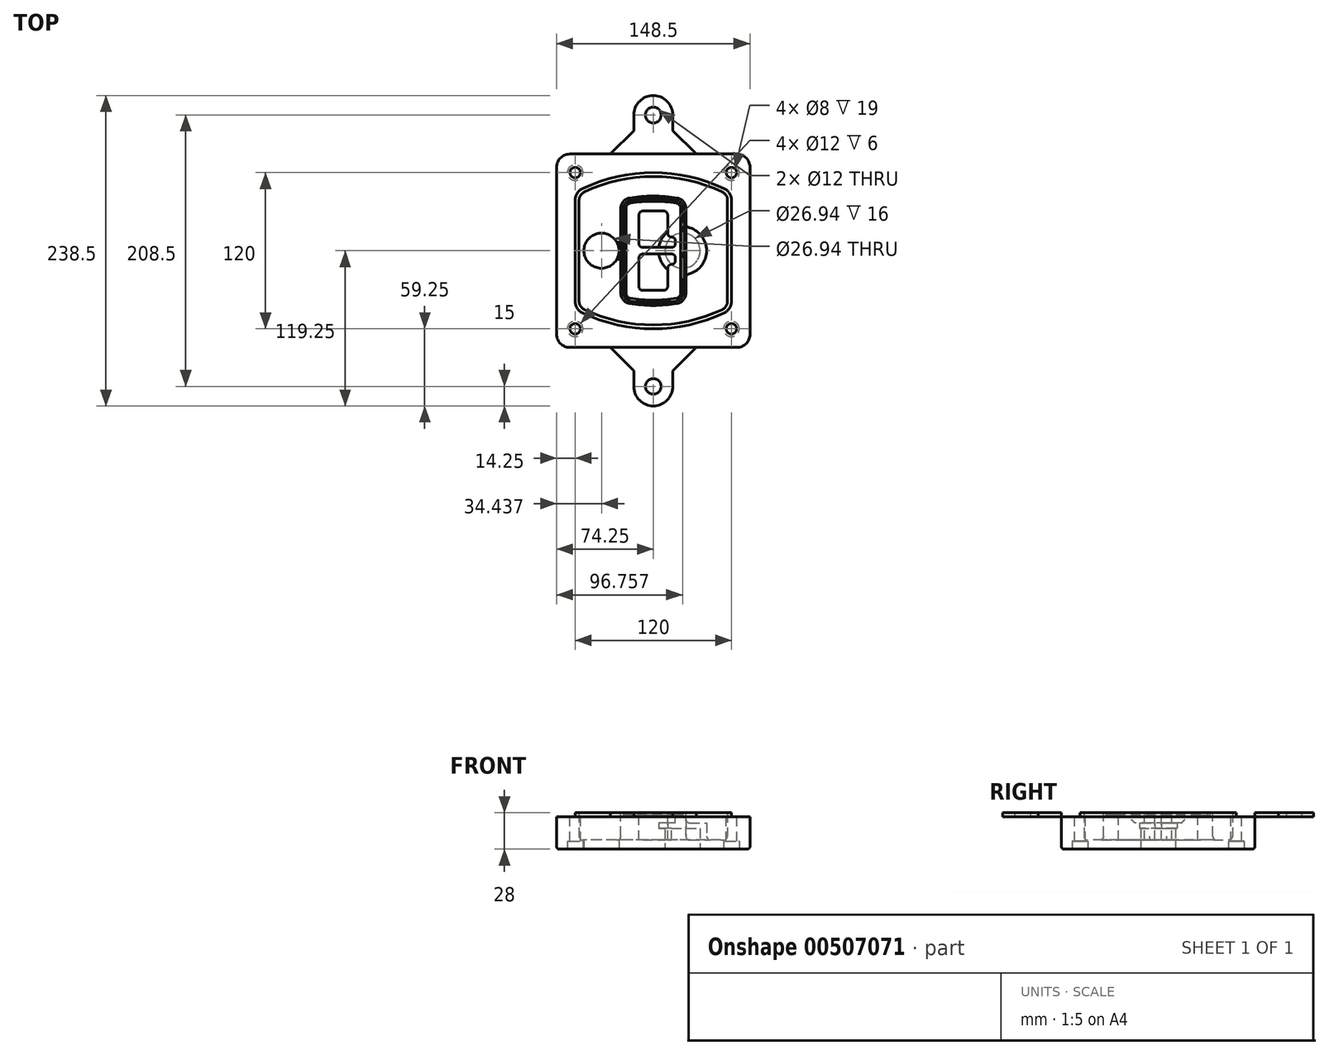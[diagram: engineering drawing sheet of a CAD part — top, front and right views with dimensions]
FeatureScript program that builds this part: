
annotation { "Feature Type Name" : "Feature", "Feature Type Description" : "" }
export const myFeature = defineFeature(function(context is Context, id is Id, definition is map)
    precondition{}
    {
        {
            var Q0;
            Q0=qCreatedBy(makeId("Top.planeOp"),FACE);
            var sketch = newSketch(context, id + "F0", { "sketchPlane" : qUnion([Q0])});
            skPoint(sketch, "E0.rect.middle", {"position": v(0, 0) * mm});
            skLineSegment(sketch, "E1.bottom", {"start": v(-64.25, -74.25) * mm, "end": v(64.25, -74.25) * mm});
            skLineSegment(sketch, "E1.top", {"start": v(-64.25, 74.25) * mm, "end": v(64.25, 74.25) * mm});
            skLineSegment(sketch, "E1.left", {"start": v(-74.25, -64.25) * mm, "end": v(-74.25, 64.25) * mm});
            skLineSegment(sketch, "E1.right", {"start": v(74.25, -64.25) * mm, "end": v(74.25, 64.25) * mm});
            skLineSegment(sketch, "E2", {"start": v(-74.25, 74.25) * mm, "end": v(74.25, -74.25) * mm, "construction": true});
            skLineSegment(sketch, "E3", {"start": v(74.25, 74.25) * mm, "end": v(-74.25, -74.25) * mm, "construction": true});
            skCircle(sketch, "E4", {"center": v(-60, 60) * mm, "radius": 4 * mm});
            skCircle(sketch, "E5", {"center": v(60, 60) * mm, "radius": 4 * mm});
            skCircle(sketch, "E6", {"center": v(60, -60) * mm, "radius": 4 * mm});
            skCircle(sketch, "E7", {"center": v(-60, -60) * mm, "radius": 4 * mm});
            skLineSegment(sketch, "E8", {"start": v(-60, 60) * mm, "end": v(60, 60) * mm, "construction": true});
            skLineSegment(sketch, "E9", {"start": v(60, 60) * mm, "end": v(60, -60) * mm, "construction": true});
            skLineSegment(sketch, "E10", {"start": v(60, -60) * mm, "end": v(-60, -60) * mm, "construction": true});
            skLineSegment(sketch, "E11", {"start": v(-60, -60) * mm, "end": v(-60, 60) * mm, "construction": true});
            skLineSegment(sketch, "E12", {"start": v(-60, 38.83) * mm, "end": v(-60, -38.83) * mm});
            skLineSegment(sketch, "E13", {"start": v(60, 38.83) * mm, "end": v(60, -38.83) * mm});
            skArc(sketch, "E14", {"start": v(54.26, 47.88) * mm, "mid": v(0, 60) * mm, "end": v(-54.26, 47.88) * mm});
            skArc(sketch, "E15", {"start": v(-54.26, -47.88) * mm, "mid": v(0, -60) * mm, "end": v(54.26, -47.88) * mm});
            skLineSegment(sketch, "E16", {"start": v(-60, 0) * mm, "end": v(60, 0) * mm, "construction": true});
            skPoint(sketch, "E17.visualSharp", {"position": v(-60, -45) * mm});
            skArc(sketch, "E17.filletArc", {"start": v(-60, -38.83) * mm, "mid": v(-58.44, -44.2) * mm, "end": v(-54.26, -47.88) * mm});
            skPoint(sketch, "E18.visualSharp", {"position": v(-60, 45) * mm});
            skArc(sketch, "E18.filletArc", {"start": v(-54.26, 47.88) * mm, "mid": v(-58.44, 44.2) * mm, "end": v(-60, 38.83) * mm});
            skPoint(sketch, "E19.visualSharp", {"position": v(60, 45) * mm});
            skArc(sketch, "E19.filletArc", {"start": v(60, 38.83) * mm, "mid": v(58.44, 44.2) * mm, "end": v(54.26, 47.88) * mm});
            skPoint(sketch, "E20.visualSharp", {"position": v(60, -45) * mm});
            skArc(sketch, "E20.filletArc", {"start": v(54.26, -47.88) * mm, "mid": v(58.44, -44.2) * mm, "end": v(60, -38.83) * mm});
            skPoint(sketch, "E21.visualSharp", {"position": v(-74.25, 74.25) * mm});
            skArc(sketch, "E21.filletArc", {"start": v(-64.25, 74.25) * mm, "mid": v(-71.32, 71.32) * mm, "end": v(-74.25, 64.25) * mm});
            skPoint(sketch, "E22.visualSharp", {"position": v(74.25, 74.25) * mm});
            skArc(sketch, "E22.filletArc", {"start": v(74.25, 64.25) * mm, "mid": v(71.32, 71.32) * mm, "end": v(64.25, 74.25) * mm});
            skPoint(sketch, "E23.visualSharp", {"position": v(74.25, -74.25) * mm});
            skArc(sketch, "E23.filletArc", {"start": v(64.25, -74.25) * mm, "mid": v(71.32, -71.32) * mm, "end": v(74.25, -64.25) * mm});
            skPoint(sketch, "E24.visualSharp", {"position": v(-74.25, -74.25) * mm});
            skArc(sketch, "E24.filletArc", {"start": v(-74.25, -64.25) * mm, "mid": v(-71.32, -71.32) * mm, "end": v(-64.25, -74.25) * mm});
            skArc(sketch, "E25.0", {"start": v(57, 38.83) * mm, "mid": v(55.9, 42.58) * mm, "end": v(52.98, 45.17) * mm});
            skLineSegment(sketch, "E25.1", {"start": v(57, 38.83) * mm, "end": v(57, -38.83) * mm});
            skArc(sketch, "E25.2", {"start": v(52.98, -45.17) * mm, "mid": v(55.9, -42.58) * mm, "end": v(57, -38.83) * mm});
            skArc(sketch, "E25.3", {"start": v(-52.98, -45.17) * mm, "mid": v(0, -57) * mm, "end": v(52.98, -45.17) * mm});
            skArc(sketch, "E25.4", {"start": v(-57, -38.83) * mm, "mid": v(-55.9, -42.58) * mm, "end": v(-52.98, -45.17) * mm});
            skArc(sketch, "E25.5", {"start": v(52.98, 45.17) * mm, "mid": v(0, 57) * mm, "end": v(-52.98, 45.17) * mm});
            skLineSegment(sketch, "E25.6", {"start": v(-57, 38.83) * mm, "end": v(-57, -38.83) * mm});
            skArc(sketch, "E25.7", {"start": v(-52.98, 45.17) * mm, "mid": v(-55.9, 42.58) * mm, "end": v(-57, 38.83) * mm});
            skArc(sketch, "E26.0", {"start": v(-55.96, 51.5) * mm, "mid": v(-61.82, 46.33) * mm, "end": v(-64, 38.83) * mm});
            skArc(sketch, "E26.1", {"start": v(55.96, 51.5) * mm, "mid": v(0, 64) * mm, "end": v(-55.96, 51.5) * mm});
            skArc(sketch, "E26.2", {"start": v(64, 38.83) * mm, "mid": v(61.82, 46.33) * mm, "end": v(55.96, 51.5) * mm});
            skLineSegment(sketch, "E26.3", {"start": v(64, 38.83) * mm, "end": v(64, -38.83) * mm});
            skArc(sketch, "E26.4", {"start": v(55.96, -51.5) * mm, "mid": v(61.82, -46.33) * mm, "end": v(64, -38.83) * mm});
            skLineSegment(sketch, "E26.5", {"start": v(-64, 38.83) * mm, "end": v(-64, -38.83) * mm});
            skArc(sketch, "E26.6", {"start": v(-55.96, -51.5) * mm, "mid": v(0, -64) * mm, "end": v(55.96, -51.5) * mm});
            skArc(sketch, "E26.7", {"start": v(-64, -38.83) * mm, "mid": v(-61.82, -46.33) * mm, "end": v(-55.96, -51.5) * mm});
            skSolve(sketch);
        }
        {
            var Q0;
            Q0=makeQuery(id+"F0.imprint","IMPRINT",FACE,{"disambiguationData":[TD([[makeQuery(id+"F0.imprint","IMPRINT",EDGE,{"derivedFrom":sQuery(id+"F0.wireOp",EDGE,"E1.bottom")}),1.0]])]});
            var Q1;
            Q1=makeQuery(id+"F0.imprint","IMPRINT",FACE,{"disambiguationData":[TD([[makeQuery(id+"F0.imprint","IMPRINT",EDGE,{"derivedFrom":sQuery(id+"F0.wireOp",EDGE,"E12")}),1.0]])]});
            var Q2;
            Q2=makeQuery(id+"F0.imprint","IMPRINT",FACE,{"disambiguationData":[TD([[makeQuery(id+"F0.imprint","IMPRINT",EDGE,{"derivedFrom":sQuery(id+"F0.wireOp",EDGE,"E25.0")}),1.0]])]});
            var Q3;
            Q3=makeQuery(id+"F0.imprint","IMPRINT",FACE,{"disambiguationData":[TD([[makeQuery(id+"F0.imprint","IMPRINT",EDGE,{"derivedFrom":sQuery(id+"F0.wireOp",EDGE,"E12")}),-1.0]])]});
            extrude(context, id + "F1", {"entities" : qUnion([Q0, Q1, Q2, Q3]), "oppositeDirection" : true, "depth" : 25 * mm});
        }
        {
            var Q0;
            Q0=makeQuery(id+"F0.imprint","IMPRINT",FACE,{"disambiguationData":[TD([[makeQuery(id+"F0.imprint","IMPRINT",EDGE,{"derivedFrom":sQuery(id+"F0.wireOp",EDGE,"E12")}),1.0]])]});
            extrude(context, id + "F2", {"entities" : qUnion([Q0]), "operationType" : NewBodyOperationType.ADD, "depth" : 3 * mm});
        }
        {
            var Q0;
            Q0=makeQuery(id+"F0.imprint","IMPRINT",FACE,{"disambiguationData":[TD([[makeQuery(id+"F0.imprint","IMPRINT",EDGE,{"derivedFrom":sQuery(id+"F0.wireOp",EDGE,"E25.0")}),1.0]])]});
            extrude(context, id + "F3", {"entities" : qUnion([Q0]), "operationType" : NewBodyOperationType.REMOVE, "oppositeDirection" : true, "depth" : 18 * mm});
        }
        {
            var Q0;
            Q0=makeQuery(id+"F2.opExtrude","CAP_FACE",FACE,{"disambiguationData":[OSD([sQuery(id+"F0.wireOp",EDGE,"E12"),sQuery(id+"F0.wireOp",EDGE,"E13"),sQuery(id+"F0.wireOp",EDGE,"E14"),sQuery(id+"F0.wireOp",EDGE,"E15"),sQuery(id+"F0.wireOp",EDGE,"E17.filletArc"),sQuery(id+"F0.wireOp",EDGE,"E18.filletArc"),sQuery(id+"F0.wireOp",EDGE,"E19.filletArc"),sQuery(id+"F0.wireOp",EDGE,"E20.filletArc"),sQuery(id+"F0.wireOp",EDGE,"E25.0"),sQuery(id+"F0.wireOp",EDGE,"E25.1"),sQuery(id+"F0.wireOp",EDGE,"E25.2"),sQuery(id+"F0.wireOp",EDGE,"E25.3"),sQuery(id+"F0.wireOp",EDGE,"E25.4"),sQuery(id+"F0.wireOp",EDGE,"E25.5"),sQuery(id+"F0.wireOp",EDGE,"E25.6"),sQuery(id+"F0.wireOp",EDGE,"E25.7")])],"isStart":false});
            var sketch = newSketch(context, id + "F4", { "sketchPlane" : qUnion([Q0])});
            skArc(sketch, "E27.0", {"start": v(-18.34, -40.45) * mm, "mid": v(0, -42) * mm, "end": v(18.34, -40.45) * mm});
            skArc(sketch, "E28.0", {"start": v(18.34, 40.45) * mm, "mid": v(0, 42) * mm, "end": v(-18.34, 40.45) * mm});
            skLineSegment(sketch, "E29", {"start": v(-25, 32.57) * mm, "end": v(-25, -32.57) * mm});
            skLineSegment(sketch, "E30", {"start": v(25, 32.57) * mm, "end": v(25, -32.57) * mm});
            skLineSegment(sketch, "E31", {"start": v(-25, 39.1) * mm, "end": v(25, 39.1) * mm, "construction": true});
            skLineSegment(sketch, "E32", {"start": v(-25, -39.1) * mm, "end": v(25, -39.1) * mm, "construction": true});
            skPoint(sketch, "E33.visualSharp", {"position": v(-25, 39.1) * mm});
            skArc(sketch, "E33.filletArc", {"start": v(-18.34, 40.45) * mm, "mid": v(-23.11, 37.73) * mm, "end": v(-25, 32.57) * mm});
            skPoint(sketch, "E34.visualSharp", {"position": v(25, 39.1) * mm});
            skArc(sketch, "E34.filletArc", {"start": v(25, 32.57) * mm, "mid": v(23.11, 37.73) * mm, "end": v(18.34, 40.45) * mm});
            skPoint(sketch, "E35.visualSharp", {"position": v(25, -39.1) * mm});
            skArc(sketch, "E35.filletArc", {"start": v(18.34, -40.45) * mm, "mid": v(23.11, -37.73) * mm, "end": v(25, -32.57) * mm});
            skPoint(sketch, "E36.visualSharp", {"position": v(-25, -39.1) * mm});
            skArc(sketch, "E36.filletArc", {"start": v(-25, -32.57) * mm, "mid": v(-23.11, -37.73) * mm, "end": v(-18.34, -40.45) * mm});
            skArc(sketch, "E37.0", {"start": v(52.98, 45.17) * mm, "mid": v(0, 57) * mm, "end": v(-52.98, 45.17) * mm});
            skArc(sketch, "E37.1", {"start": v(-52.98, 45.17) * mm, "mid": v(-55.9, 42.58) * mm, "end": v(-57, 38.83) * mm});
            skLineSegment(sketch, "E37.2", {"start": v(-57, 38.83) * mm, "end": v(-57, -38.83) * mm});
            skArc(sketch, "E37.3", {"start": v(-57, -38.83) * mm, "mid": v(-55.9, -42.58) * mm, "end": v(-52.98, -45.17) * mm});
            skArc(sketch, "E37.4", {"start": v(-52.98, -45.17) * mm, "mid": v(0, -57) * mm, "end": v(52.98, -45.17) * mm});
            skArc(sketch, "E37.5", {"start": v(52.98, -45.17) * mm, "mid": v(55.9, -42.58) * mm, "end": v(57, -38.83) * mm});
            skLineSegment(sketch, "E37.6", {"start": v(57, 38.83) * mm, "end": v(57, -38.83) * mm});
            skArc(sketch, "E37.7", {"start": v(57, 38.83) * mm, "mid": v(55.9, 42.58) * mm, "end": v(52.98, 45.17) * mm});
            skLineSegment(sketch, "E38.0", {"start": v(23, 32.57) * mm, "end": v(23, -32.57) * mm});
            skArc(sketch, "E38.1", {"start": v(18, -38.48) * mm, "mid": v(21.58, -36.44) * mm, "end": v(23, -32.57) * mm});
            skArc(sketch, "E38.2", {"start": v(-18, -38.48) * mm, "mid": v(0, -40) * mm, "end": v(18, -38.48) * mm});
            skArc(sketch, "E38.3", {"start": v(-23, -32.57) * mm, "mid": v(-21.58, -36.44) * mm, "end": v(-18, -38.48) * mm});
            skLineSegment(sketch, "E38.4", {"start": v(-23, 32.57) * mm, "end": v(-23, -32.57) * mm});
            skArc(sketch, "E38.5", {"start": v(23, 32.57) * mm, "mid": v(21.58, 36.44) * mm, "end": v(18, 38.48) * mm});
            skArc(sketch, "E38.6", {"start": v(-18, 38.48) * mm, "mid": v(-21.58, 36.44) * mm, "end": v(-23, 32.57) * mm});
            skArc(sketch, "E38.7", {"start": v(18, 38.48) * mm, "mid": v(0, 40) * mm, "end": v(-18, 38.48) * mm});
            skArc(sketch, "E39.0", {"start": v(21, 32.57) * mm, "mid": v(20.06, 35.15) * mm, "end": v(17.67, 36.5) * mm});
            skLineSegment(sketch, "E39.1", {"start": v(21, 32.57) * mm, "end": v(21, -32.57) * mm});
            skArc(sketch, "E39.2", {"start": v(17.67, -36.5) * mm, "mid": v(20.06, -35.15) * mm, "end": v(21, -32.57) * mm});
            skArc(sketch, "E39.3", {"start": v(-17.67, -36.5) * mm, "mid": v(0, -38) * mm, "end": v(17.67, -36.5) * mm});
            skArc(sketch, "E39.4", {"start": v(-21, -32.57) * mm, "mid": v(-20.06, -35.15) * mm, "end": v(-17.67, -36.5) * mm});
            skArc(sketch, "E39.5", {"start": v(17.67, 36.5) * mm, "mid": v(0, 38) * mm, "end": v(-17.67, 36.5) * mm});
            skLineSegment(sketch, "E39.6", {"start": v(-21, 32.57) * mm, "end": v(-21, -32.57) * mm});
            skArc(sketch, "E39.7", {"start": v(-17.67, 36.5) * mm, "mid": v(-20.06, 35.15) * mm, "end": v(-21, 32.57) * mm});
            skLineSegment(sketch, "E40", {"start": v(-25, 0) * mm, "end": v(25, 0) * mm, "construction": true});
            skLineSegment(sketch, "E41", {"start": v(-11, 5.5) * mm, "end": v(-11, 27.5) * mm});
            skLineSegment(sketch, "E42", {"start": v(-8, 30.5) * mm, "end": v(8, 30.5) * mm});
            skLineSegment(sketch, "E43", {"start": v(11, 27.5) * mm, "end": v(11, 13.5) * mm});
            skLineSegment(sketch, "E44", {"start": v(14, 10.5) * mm, "end": v(14, 10.5) * mm});
            skLineSegment(sketch, "E45", {"start": v(17, 7.5) * mm, "end": v(17, 5.5) * mm});
            skLineSegment(sketch, "E46", {"start": v(14, 2.5) * mm, "end": v(-8, 2.5) * mm});
            skPoint(sketch, "E47.visualSharp", {"position": v(-11, 30.5) * mm});
            skArc(sketch, "E47.filletArc", {"start": v(-8, 30.5) * mm, "mid": v(-10.12, 29.62) * mm, "end": v(-11, 27.5) * mm});
            skPoint(sketch, "E48.visualSharp", {"position": v(11, 30.5) * mm});
            skArc(sketch, "E48.filletArc", {"start": v(11, 27.5) * mm, "mid": v(10.12, 29.62) * mm, "end": v(8, 30.5) * mm});
            skPoint(sketch, "E49.visualSharp", {"position": v(11, 10.5) * mm});
            skArc(sketch, "E49.filletArc", {"start": v(11, 13.5) * mm, "mid": v(11.88, 11.38) * mm, "end": v(14, 10.5) * mm});
            skPoint(sketch, "E50.visualSharp", {"position": v(17, 10.5) * mm});
            skArc(sketch, "E50.filletArc", {"start": v(17, 7.5) * mm, "mid": v(16.12, 9.62) * mm, "end": v(14, 10.5) * mm});
            skPoint(sketch, "E51.visualSharp", {"position": v(17, 2.5) * mm});
            skArc(sketch, "E51.filletArc", {"start": v(14, 2.5) * mm, "mid": v(16.12, 3.38) * mm, "end": v(17, 5.5) * mm});
            skPoint(sketch, "E52.visualSharp", {"position": v(-11, 2.5) * mm});
            skArc(sketch, "E52.filletArc", {"start": v(-11, 5.5) * mm, "mid": v(-10.12, 3.38) * mm, "end": v(-8, 2.5) * mm});
            skLineSegment(sketch, "E53.0.MirrorCS", {"start": v(14, -2.5) * mm, "end": v(-8, -2.5) * mm});
            skArc(sketch, "E54.0.MirrorCS", {"start": v(-11, -5.5) * mm, "mid": v(-10.12, -3.38) * mm, "end": v(-8, -2.5) * mm});
            skLineSegment(sketch, "E55.0.MirrorCS", {"start": v(-11, -5.5) * mm, "end": v(-11, -27.5) * mm});
            skArc(sketch, "E56.0.MirrorCS", {"start": v(-8, -30.5) * mm, "mid": v(-10.12, -29.62) * mm, "end": v(-11, -27.5) * mm});
            skLineSegment(sketch, "E57.0.MirrorCS", {"start": v(-8, -30.5) * mm, "end": v(8, -30.5) * mm});
            skArc(sketch, "E58.0.MirrorCS", {"start": v(11, -27.5) * mm, "mid": v(10.12, -29.62) * mm, "end": v(8, -30.5) * mm});
            skLineSegment(sketch, "E59.0.MirrorCS", {"start": v(11, -27.5) * mm, "end": v(11, -13.5) * mm});
            skArc(sketch, "E60.0.MirrorCS", {"start": v(11, -13.5) * mm, "mid": v(11.88, -11.38) * mm, "end": v(14, -10.5) * mm});
            skArc(sketch, "E61.0.MirrorCS", {"start": v(17, -7.5) * mm, "mid": v(16.12, -9.62) * mm, "end": v(14, -10.5) * mm});
            skLineSegment(sketch, "E62.0.MirrorCS", {"start": v(17, -7.5) * mm, "end": v(17, -5.5) * mm});
            skArc(sketch, "E63.0.MirrorCS", {"start": v(14, -2.5) * mm, "mid": v(16.12, -3.38) * mm, "end": v(17, -5.5) * mm});
            skSolve(sketch);
        }
        {
            var Q0;
            Q0=makeQuery(id+"F4.imprint","IMPRINT",FACE,{"disambiguationData":[TD([[makeQuery(id+"F4.imprint","IMPRINT",EDGE,{"derivedFrom":sQuery(id+"F4.wireOp",EDGE,"E27.0")}),1.0]])]});
            var Q1;
            Q1=makeQuery(id+"F4.imprint","IMPRINT",FACE,{"disambiguationData":[TD([[makeQuery(id+"F4.imprint","IMPRINT",EDGE,{"derivedFrom":sQuery(id+"F4.wireOp",EDGE,"E38.0")}),-1.0]])]});
            var Q2;
            Q2=makeQuery(id+"F4.imprint","IMPRINT",FACE,{"disambiguationData":[TD([[makeQuery(id+"F4.imprint","IMPRINT",EDGE,{"derivedFrom":sQuery(id+"F4.wireOp",EDGE,"E39.0")}),1.0]])]});
            extrude(context, id + "F5", {"entities" : qUnion([Q0, Q1, Q2]), "operationType" : NewBodyOperationType.ADD, "endBound" : BoundingType.UP_TO_NEXT, "oppositeDirection" : true, "depth" : 25 * mm});
        }
        {
            var Q0;
            Q0=makeQuery(id+"F4.imprint","IMPRINT",FACE,{"disambiguationData":[TD([[makeQuery(id+"F4.imprint","IMPRINT",EDGE,{"derivedFrom":sQuery(id+"F4.wireOp",EDGE,"E38.0")}),-1.0]])]});
            extrude(context, id + "F6", {"entities" : qUnion([Q0]), "operationType" : NewBodyOperationType.REMOVE, "oppositeDirection" : true, "depth" : 2 * mm});
        }
        {
            var Q0;
            Q0=makeQuery(id+"F1.opExtrude","CAP_FACE",FACE,{"disambiguationData":[OSD([sQuery(id+"F0.wireOp",EDGE,"E1.bottom"),sQuery(id+"F0.wireOp",EDGE,"E1.top"),sQuery(id+"F0.wireOp",EDGE,"E1.left"),sQuery(id+"F0.wireOp",EDGE,"E1.right"),sQuery(id+"F0.wireOp",EDGE,"E4"),sQuery(id+"F0.wireOp",EDGE,"E5"),sQuery(id+"F0.wireOp",EDGE,"E6"),sQuery(id+"F0.wireOp",EDGE,"E7"),sQuery(id+"F0.wireOp",EDGE,"E21.filletArc"),sQuery(id+"F0.wireOp",EDGE,"E22.filletArc"),sQuery(id+"F0.wireOp",EDGE,"E23.filletArc"),sQuery(id+"F0.wireOp",EDGE,"E24.filletArc")])],"isStart":false});
            var sketch = newSketch(context, id + "F7", { "sketchPlane" : qUnion([Q0])});
            skCircle(sketch, "E64", {"center": v(22.5, 0) * mm, "radius": 13.47 * mm});
            skCircle(sketch, "E65", {"center": v(-39.81, 0) * mm, "radius": 13.47 * mm});
            skLineSegment(sketch, "E66", {"start": v(74.25, 0) * mm, "end": v(-74.25, 0) * mm});
            skCircle(sketch, "E67", {"center": v(22.5, 0) * mm, "radius": 18.47 * mm});
            skCircle(sketch, "E68", {"center": v(60, -60) * mm, "radius": 6 * mm});
            skCircle(sketch, "E69", {"center": v(-60, -60) * mm, "radius": 6 * mm});
            skCircle(sketch, "E70", {"center": v(-60, 60) * mm, "radius": 6 * mm});
            skCircle(sketch, "E71", {"center": v(60, 60) * mm, "radius": 6 * mm});
            skSolve(sketch);
        }
        {
            var Q0;
            {var subQ1=sQuery(id+"F7.wireOp",EDGE,"E66");var subQ4=sQuery(id+"F7.wireOp",EDGE,"E64");var subQ6=makeQuery(id+"F7.imprint","INTERSECT",VERTEX,{"disambiguationData":[OD(0.0)],"derivedFrom":[subQ4,subQ1]});Q0=makeQuery(id+"F7.imprint","IMPRINT",FACE,{"disambiguationData":[TD([[makeQuery(id+"F7.imprint","IMPRINT",EDGE,{"disambiguationData":[TD([[subQ6,-1.0]])],"derivedFrom":subQ4}),-1.0]])]});}
            var Q1;
            {var subQ0=sQuery(id+"F7.wireOp",EDGE,"E66");var subQ1=sQuery(id+"F7.wireOp",EDGE,"E64");var subQ3=makeQuery(id+"F7.imprint","INTERSECT",VERTEX,{"disambiguationData":[OD(0.0)],"derivedFrom":[subQ1,subQ0]});Q1=makeQuery(id+"F7.imprint","IMPRINT",FACE,{"disambiguationData":[TD([[makeQuery(id+"F7.imprint","IMPRINT",EDGE,{"disambiguationData":[TD([[subQ3,-1.0]])],"derivedFrom":subQ1}),1.0]])]});}
            var Q2;
            {var subQ0=sQuery(id+"F7.wireOp",EDGE,"E66");var subQ1=sQuery(id+"F7.wireOp",EDGE,"E64");var subQ3=makeQuery(id+"F7.imprint","INTERSECT",VERTEX,{"disambiguationData":[OD(0.0)],"derivedFrom":[subQ1,subQ0]});Q2=makeQuery(id+"F7.imprint","IMPRINT",FACE,{"disambiguationData":[TD([[makeQuery(id+"F7.imprint","IMPRINT",EDGE,{"disambiguationData":[TD([[subQ3,1.0]])],"derivedFrom":subQ1}),1.0]])]});}
            var Q3;
            {var subQ1=sQuery(id+"F7.wireOp",EDGE,"E66");var subQ4=sQuery(id+"F7.wireOp",EDGE,"E64");var subQ6=makeQuery(id+"F7.imprint","INTERSECT",VERTEX,{"disambiguationData":[OD(0.0)],"derivedFrom":[subQ4,subQ1]});Q3=makeQuery(id+"F7.imprint","IMPRINT",FACE,{"disambiguationData":[TD([[makeQuery(id+"F7.imprint","IMPRINT",EDGE,{"disambiguationData":[TD([[subQ6,1.0]])],"derivedFrom":subQ4}),-1.0]])]});}
            extrude(context, id + "F8", {"entities" : qUnion([Q0, Q1, Q2, Q3]), "operationType" : NewBodyOperationType.ADD, "oppositeDirection" : true, "depth" : 20 * mm});
        }
        {
            var Q0;
            {var subQ0=sQuery(id+"F7.wireOp",EDGE,"E66");var subQ1=sQuery(id+"F7.wireOp",EDGE,"E64");var subQ3=makeQuery(id+"F7.imprint","INTERSECT",VERTEX,{"disambiguationData":[OD(0.0)],"derivedFrom":[subQ1,subQ0]});Q0=makeQuery(id+"F7.imprint","IMPRINT",FACE,{"disambiguationData":[TD([[makeQuery(id+"F7.imprint","IMPRINT",EDGE,{"disambiguationData":[TD([[subQ3,-1.0]])],"derivedFrom":subQ1}),1.0]])]});}
            var Q1;
            {var subQ0=sQuery(id+"F7.wireOp",EDGE,"E66");var subQ1=sQuery(id+"F7.wireOp",EDGE,"E64");var subQ3=makeQuery(id+"F7.imprint","INTERSECT",VERTEX,{"disambiguationData":[OD(0.0)],"derivedFrom":[subQ1,subQ0]});Q1=makeQuery(id+"F7.imprint","IMPRINT",FACE,{"disambiguationData":[TD([[makeQuery(id+"F7.imprint","IMPRINT",EDGE,{"disambiguationData":[TD([[subQ3,1.0]])],"derivedFrom":subQ1}),1.0]])]});}
            extrude(context, id + "F9", {"entities" : qUnion([Q0, Q1]), "operationType" : NewBodyOperationType.REMOVE, "oppositeDirection" : true, "depth" : 16 * mm});
        }
        {
            var Q0;
            {var subQ0=sQuery(id+"F7.wireOp",EDGE,"E66");var subQ1=sQuery(id+"F7.wireOp",EDGE,"E65");var subQ3=makeQuery(id+"F7.imprint","INTERSECT",VERTEX,{"disambiguationData":[OD(0.0)],"derivedFrom":[subQ1,subQ0]});Q0=makeQuery(id+"F7.imprint","IMPRINT",FACE,{"disambiguationData":[TD([[makeQuery(id+"F7.imprint","IMPRINT",EDGE,{"disambiguationData":[TD([[subQ3,-1.0]])],"derivedFrom":subQ1}),1.0]])]});}
            var Q1;
            {var subQ0=sQuery(id+"F7.wireOp",EDGE,"E66");var subQ1=sQuery(id+"F7.wireOp",EDGE,"E65");var subQ3=makeQuery(id+"F7.imprint","INTERSECT",VERTEX,{"disambiguationData":[OD(0.0)],"derivedFrom":[subQ1,subQ0]});Q1=makeQuery(id+"F7.imprint","IMPRINT",FACE,{"disambiguationData":[TD([[makeQuery(id+"F7.imprint","IMPRINT",EDGE,{"disambiguationData":[TD([[subQ3,1.0]])],"derivedFrom":subQ1}),1.0]])]});}
            var Q2;
            {var subQ0=sQuery(id+"F0.wireOp",EDGE,"E21.filletArc");var subQ1=sQuery(id+"F0.wireOp",EDGE,"E7");var subQ2=sQuery(id+"F0.wireOp",EDGE,"E6");var subQ3=sQuery(id+"F0.wireOp",EDGE,"E5");var subQ4=sQuery(id+"F0.wireOp",EDGE,"E4");var subQ5=sQuery(id+"F0.wireOp",EDGE,"E22.filletArc");var subQ6=sQuery(id+"F0.wireOp",EDGE,"E1.bottom");var subQ7=sQuery(id+"F0.wireOp",EDGE,"E1.right");var subQ8=sQuery(id+"F0.wireOp",EDGE,"E1.top");var subQ9=sQuery(id+"F0.wireOp",EDGE,"E1.left");var subQ10=sQuery(id+"F0.wireOp",EDGE,"E23.filletArc");var subQ11=sQuery(id+"F0.wireOp",EDGE,"E24.filletArc");Q2=makeQuery(id+"F2.boolean.opBoolean","SPLIT",FACE,{"disambiguationData":[TD([makeQuery(id+"F1.opExtrude","SWEPT_FACE",FACE,{"disambiguationData":[OSD([subQ6])]})])],"derivedFrom":makeQuery(id+"F1.opExtrude","CAP_FACE",FACE,{"disambiguationData":[OSD([subQ6,subQ8,subQ9,subQ7,subQ4,subQ3,subQ2,subQ1,subQ0,subQ5,subQ10,subQ11])],"isStart":true})});}
            extrude(context, id + "F10", {"entities" : qUnion([Q0, Q1, Q2]), "operationType" : NewBodyOperationType.REMOVE, "oppositeDirection" : true, "depth" : 25 * mm});
        }
        {
            var Q0;
            Q0=makeQuery(id+"F7.imprint","IMPRINT",FACE,{"disambiguationData":[TD([[makeQuery(id+"F7.imprint","IMPRINT",EDGE,{"derivedFrom":sQuery(id+"F7.wireOp",EDGE,"E68")}),1.0]])]});
            var Q1;
            Q1=makeQuery(id+"F7.imprint","IMPRINT",FACE,{"disambiguationData":[TD([[makeQuery(id+"F7.imprint","IMPRINT",EDGE,{"derivedFrom":makeQuery(id+"F1.opExtrude","CAP_EDGE",EDGE,{"disambiguationData":[OSD([sQuery(id+"F0.wireOp",EDGE,"E5")])],"isStart":false})}),-1.0]])]});
            var Q2;
            Q2=makeQuery(id+"F7.imprint","IMPRINT",FACE,{"disambiguationData":[TD([[makeQuery(id+"F7.imprint","IMPRINT",EDGE,{"derivedFrom":sQuery(id+"F7.wireOp",EDGE,"E69")}),1.0]])]});
            var Q3;
            Q3=makeQuery(id+"F7.imprint","IMPRINT",FACE,{"disambiguationData":[TD([[makeQuery(id+"F7.imprint","IMPRINT",EDGE,{"derivedFrom":makeQuery(id+"F1.opExtrude","CAP_EDGE",EDGE,{"disambiguationData":[OSD([sQuery(id+"F0.wireOp",EDGE,"E4")])],"isStart":false})}),-1.0]])]});
            var Q4;
            Q4=makeQuery(id+"F7.imprint","IMPRINT",FACE,{"disambiguationData":[TD([[makeQuery(id+"F7.imprint","IMPRINT",EDGE,{"derivedFrom":sQuery(id+"F7.wireOp",EDGE,"E70")}),1.0]])]});
            var Q5;
            Q5=makeQuery(id+"F7.imprint","IMPRINT",FACE,{"disambiguationData":[TD([[makeQuery(id+"F7.imprint","IMPRINT",EDGE,{"derivedFrom":makeQuery(id+"F1.opExtrude","CAP_EDGE",EDGE,{"disambiguationData":[OSD([sQuery(id+"F0.wireOp",EDGE,"E7")])],"isStart":false})}),-1.0]])]});
            var Q6;
            Q6=makeQuery(id+"F7.imprint","IMPRINT",FACE,{"disambiguationData":[TD([[makeQuery(id+"F7.imprint","IMPRINT",EDGE,{"derivedFrom":sQuery(id+"F7.wireOp",EDGE,"E71")}),1.0]])]});
            var Q7;
            Q7=makeQuery(id+"F7.imprint","IMPRINT",FACE,{"disambiguationData":[TD([[makeQuery(id+"F7.imprint","IMPRINT",EDGE,{"derivedFrom":makeQuery(id+"F1.opExtrude","CAP_EDGE",EDGE,{"disambiguationData":[OSD([sQuery(id+"F0.wireOp",EDGE,"E6")])],"isStart":false})}),-1.0]])]});
            extrude(context, id + "F11", {"entities" : qUnion([Q0, Q1, Q2, Q3, Q4, Q5, Q6, Q7]), "operationType" : NewBodyOperationType.REMOVE, "oppositeDirection" : true, "depth" : 6 * mm});
        }
        {
            var Q0;
            Q0=makeQuery(id+"F9.boolean.opBoolean","COPY",FACE,{"derivedFrom":makeQuery(id+"F9.opExtrude","CAP_FACE",FACE,{"disambiguationData":[OSD([sQuery(id+"F7.wireOp",EDGE,"E64")])],"isStart":false})});
            var sketch = newSketch(context, id + "F12", { "sketchPlane" : qUnion([Q0])});
            skArc(sketch, "E72.0", {"start": v(11, 14.45) * mm, "mid": v(6.45, 9.13) * mm, "end": v(4.2, 2.5) * mm});
            skArc(sketch, "E72.1", {"start": v(4.2, -2.5) * mm, "mid": v(6.45, -9.13) * mm, "end": v(11, -14.45) * mm});
            skLineSegment(sketch, "E73", {"start": v(4.2, -2.5) * mm, "end": v(14, -2.5) * mm});
            skLineSegment(sketch, "E74.0", {"start": v(14, 2.5) * mm, "end": v(4.2, 2.5) * mm});
            skArc(sketch, "E74.1", {"start": v(14, 2.5) * mm, "mid": v(16.12, 3.38) * mm, "end": v(17, 5.5) * mm});
            skLineSegment(sketch, "E74.2", {"start": v(17, 7.5) * mm, "end": v(17, 5.5) * mm});
            skArc(sketch, "E74.3", {"start": v(17, 7.5) * mm, "mid": v(16.12, 9.62) * mm, "end": v(14, 10.5) * mm});
            skArc(sketch, "E74.4", {"start": v(11, 13.5) * mm, "mid": v(11.88, 11.38) * mm, "end": v(14, 10.5) * mm});
            skLineSegment(sketch, "E74.5", {"start": v(11, 14.45) * mm, "end": v(11, 13.5) * mm});
            skLineSegment(sketch, "E74.7", {"start": v(14, -2.5) * mm, "end": v(4.2, -2.5) * mm});
            skArc(sketch, "E74.8", {"start": v(14, -2.5) * mm, "mid": v(16.12, -3.38) * mm, "end": v(17, -5.5) * mm});
            skLineSegment(sketch, "E74.9", {"start": v(17, -7.5) * mm, "end": v(17, -5.5) * mm});
            skArc(sketch, "E74.10", {"start": v(17, -7.5) * mm, "mid": v(16.12, -9.62) * mm, "end": v(14, -10.5) * mm});
            skArc(sketch, "E74.11", {"start": v(11, -13.5) * mm, "mid": v(11.88, -11.38) * mm, "end": v(14, -10.5) * mm});
            skLineSegment(sketch, "E74.12", {"start": v(11, -14.45) * mm, "end": v(11, -13.5) * mm});
            skPoint(sketch, "E75.orphan", {"position": v(11, -27.5) * mm});
            skPoint(sketch, "E76.orphan", {"position": v(-8, -2.5) * mm});
            skPoint(sketch, "E77.orphan", {"position": v(-8, 2.5) * mm});
            skPoint(sketch, "E78.orphan", {"position": v(11, 27.5) * mm});
            skSolve(sketch);
        }
        {
            var Q0;
            {var subQ7=sQuery(id+"F12.wireOp",EDGE,"E72.0");var subQ14=sQuery(id+"F12.wireOp",EDGE,"E72.1");var subQ16=sQuery(id+"F12.wireOp",EDGE,"E74.1");var subQ18=sQuery(id+"F12.wireOp",EDGE,"E74.8");Q0=qUnion([makeQuery(id+"F12.imprint","IMPRINT",FACE,{"disambiguationData":[TD([[makeQuery(id+"F12.imprint","IMPRINT",EDGE,{"derivedFrom":subQ7}),1.0]])]}),makeQuery(id+"F12.imprint","IMPRINT",FACE,{"disambiguationData":[TD([[makeQuery(id+"F12.imprint","IMPRINT",EDGE,{"derivedFrom":subQ14}),1.0]])]}),makeQuery(id+"F12.imprint","IMPRINT",FACE,{"disambiguationData":[TD([[makeQuery(id+"F12.imprint","IMPRINT",EDGE,{"derivedFrom":subQ16}),1.0]])]}),makeQuery(id+"F12.imprint","IMPRINT",FACE,{"disambiguationData":[TD([[makeQuery(id+"F12.imprint","IMPRINT",EDGE,{"derivedFrom":subQ18}),-1.0]])]})]);}
            var Q1;
            Q1=makeQuery(id+"F5.boolean.opBoolean","SPLIT",FACE,{"disambiguationData":[TD([makeQuery(id+"F5.opExtrude","SWEPT_FACE",FACE,{"disambiguationData":[OSD([sQuery(id+"F4.wireOp",EDGE,"E41")])]})])],"derivedFrom":makeQuery(id+"F3.boolean.opBoolean","COPY",FACE,{"derivedFrom":makeQuery(id+"F3.opExtrude","CAP_FACE",FACE,{"disambiguationData":[OSD([sQuery(id+"F0.wireOp",EDGE,"E25.0"),sQuery(id+"F0.wireOp",EDGE,"E25.1"),sQuery(id+"F0.wireOp",EDGE,"E25.2"),sQuery(id+"F0.wireOp",EDGE,"E25.3"),sQuery(id+"F0.wireOp",EDGE,"E25.4"),sQuery(id+"F0.wireOp",EDGE,"E25.5"),sQuery(id+"F0.wireOp",EDGE,"E25.6"),sQuery(id+"F0.wireOp",EDGE,"E25.7")])],"isStart":false})})});
            extrude(context, id + "F13", {"entities" : qUnion([Q0]), "operationType" : NewBodyOperationType.REMOVE, "endBound" : BoundingType.UP_TO_SURFACE, "endBoundEntityFace" : qUnion([Q1]), "depth" : 25 * mm});
        }
        {
            var Q0;
            Q0=makeQuery(id+"F3.boolean.opBoolean","COPY",EDGE,{"derivedFrom":makeQuery(id+"F3.opExtrude","CAP_EDGE",EDGE,{"disambiguationData":[OSD([sQuery(id+"F0.wireOp",EDGE,"E25.6")])],"isStart":false})});
            var Q1;
            Q1=makeQuery(id+"F8.boolean.opBoolean","INTERSECT",EDGE,{"derivedFrom":[makeQuery(id+"F5.opExtrude","SWEPT_FACE",FACE,{"disambiguationData":[OSD([sQuery(id+"F4.wireOp",EDGE,"E30")])]}),makeQuery(id+"F8.opExtrude","CAP_FACE",FACE,{"disambiguationData":[OSD([sQuery(id+"F7.wireOp",EDGE,"E67")])],"isStart":false})]});
            var Q2;
            Q2=makeQuery(id+"F8.boolean.opBoolean","INTERSECT",EDGE,{"disambiguationData":[OD(1.0)],"derivedFrom":[makeQuery(id+"F5.opExtrude","SWEPT_FACE",FACE,{"disambiguationData":[OSD([sQuery(id+"F4.wireOp",EDGE,"E30")])]}),makeQuery(id+"F8.opExtrude","SWEPT_FACE",FACE,{"disambiguationData":[OSD([sQuery(id+"F7.wireOp",EDGE,"E67")])]})]});
            var Q3;
            {var subQ0=sQuery(id+"F4.wireOp",EDGE,"E30");Q3=makeQuery(id+"F8.boolean.opBoolean","SPLIT",EDGE,{"disambiguationData":[TD([makeQuery(id+"F5.opExtrude","SWEPT_FACE",FACE,{"disambiguationData":[OSD([sQuery(id+"F4.wireOp",EDGE,"E35.filletArc")])]})])],"derivedFrom":makeQuery(id+"F5.opExtrude","CAP_EDGE",EDGE,{"disambiguationData":[OSD([subQ0])],"isStart":false})});}
            var Q4;
            {var subQ0=sQuery(id+"F0.wireOp",EDGE,"E25.7");var subQ1=sQuery(id+"F0.wireOp",EDGE,"E25.1");var subQ2=sQuery(id+"F0.wireOp",EDGE,"E25.6");var subQ3=sQuery(id+"F0.wireOp",EDGE,"E25.5");var subQ4=sQuery(id+"F0.wireOp",EDGE,"E25.4");var subQ5=sQuery(id+"F0.wireOp",EDGE,"E25.0");var subQ6=sQuery(id+"F0.wireOp",EDGE,"E25.2");var subQ7=sQuery(id+"F0.wireOp",EDGE,"E25.3");Q4=makeQuery(id+"F8.boolean.opBoolean","INTERSECT",EDGE,{"derivedFrom":[makeQuery(id+"F5.boolean.opBoolean","SPLIT",FACE,{"disambiguationData":[TD([makeQuery(id+"F2.opExtrude","SWEPT_FACE",FACE,{"disambiguationData":[OSD([subQ5])]})])],"derivedFrom":makeQuery(id+"F3.boolean.opBoolean","COPY",FACE,{"derivedFrom":makeQuery(id+"F3.opExtrude","CAP_FACE",FACE,{"disambiguationData":[OSD([subQ5,subQ1,subQ6,subQ7,subQ4,subQ3,subQ2,subQ0])],"isStart":false})})}),makeQuery(id+"F8.opExtrude","SWEPT_FACE",FACE,{"disambiguationData":[OSD([sQuery(id+"F7.wireOp",EDGE,"E67")])]})]});}
            var Q5;
            Q5=makeQuery(id+"F8.boolean.opBoolean","INTERSECT",EDGE,{"disambiguationData":[OD(0.0)],"derivedFrom":[makeQuery(id+"F5.opExtrude","SWEPT_FACE",FACE,{"disambiguationData":[OSD([sQuery(id+"F4.wireOp",EDGE,"E30")])]}),makeQuery(id+"F8.opExtrude","SWEPT_FACE",FACE,{"disambiguationData":[OSD([sQuery(id+"F7.wireOp",EDGE,"E67")])]})]});
            fillet(context, id + "F14", {"entities" : qUnion([Q0, Q1, Q2, Q3, Q4, Q5]), "radius" : 3 * mm, "tangentPropagation" : true, "allowEdgeOverflow" : false});
        }
        {
            var Q0;
            Q0=makeQuery(id+"F1.opExtrude","CAP_EDGE",EDGE,{"disambiguationData":[OSD([sQuery(id+"F0.wireOp",EDGE,"E1.bottom")])],"isStart":false});
            fillet(context, id + "F15", {"entities" : qUnion([Q0]), "radius" : 2 * mm, "tangentPropagation" : true, "allowEdgeOverflow" : false});
        }
        {
            var Q0;
            {var subQ0=sQuery(id+"F0.wireOp",EDGE,"E21.filletArc");var subQ1=sQuery(id+"F0.wireOp",EDGE,"E7");var subQ2=sQuery(id+"F0.wireOp",EDGE,"E6");var subQ3=sQuery(id+"F0.wireOp",EDGE,"E5");var subQ4=sQuery(id+"F0.wireOp",EDGE,"E4");var subQ5=sQuery(id+"F0.wireOp",EDGE,"E22.filletArc");var subQ6=sQuery(id+"F0.wireOp",EDGE,"E1.bottom");var subQ7=sQuery(id+"F0.wireOp",EDGE,"E1.right");var subQ8=sQuery(id+"F0.wireOp",EDGE,"E1.top");var subQ9=sQuery(id+"F0.wireOp",EDGE,"E1.left");var subQ10=sQuery(id+"F0.wireOp",EDGE,"E23.filletArc");var subQ11=sQuery(id+"F0.wireOp",EDGE,"E24.filletArc");Q0=makeQuery(id+"F2.boolean.opBoolean","SPLIT",FACE,{"disambiguationData":[TD([makeQuery(id+"F1.opExtrude","SWEPT_FACE",FACE,{"disambiguationData":[OSD([subQ6])]})])],"derivedFrom":makeQuery(id+"F1.opExtrude","CAP_FACE",FACE,{"disambiguationData":[OSD([subQ6,subQ8,subQ9,subQ7,subQ4,subQ3,subQ2,subQ1,subQ0,subQ5,subQ10,subQ11])],"isStart":true})});}
            var sketch = newSketch(context, id + "F16", { "sketchPlane" : qUnion([Q0])});
            skLineSegment(sketch, "E79.0", {"start": v(-64.25, 74.25) * mm, "end": v(64.25, 74.25) * mm});
            skArc(sketch, "E79.1", {"start": v(-64.25, 74.25) * mm, "mid": v(-71.32, 71.32) * mm, "end": v(-74.25, 64.25) * mm});
            skArc(sketch, "E79.2", {"start": v(74.25, 64.25) * mm, "mid": v(71.32, 71.32) * mm, "end": v(64.25, 74.25) * mm});
            skLineSegment(sketch, "E79.3", {"start": v(74.25, -64.25) * mm, "end": v(74.25, 64.25) * mm});
            skArc(sketch, "E79.4", {"start": v(64.25, -74.25) * mm, "mid": v(71.32, -71.32) * mm, "end": v(74.25, -64.25) * mm});
            skLineSegment(sketch, "E79.5", {"start": v(-64.25, -74.25) * mm, "end": v(64.25, -74.25) * mm});
            skArc(sketch, "E79.6", {"start": v(-74.25, -64.25) * mm, "mid": v(-71.32, -71.32) * mm, "end": v(-64.25, -74.25) * mm});
            skCircle(sketch, "E79.7", {"center": v(-60, -60) * mm, "radius": 4 * mm});
            skCircle(sketch, "E79.8", {"center": v(60, -60) * mm, "radius": 4 * mm});
            skCircle(sketch, "E79.9", {"center": v(60, 60) * mm, "radius": 4 * mm});
            skCircle(sketch, "E79.10", {"center": v(-60, 60) * mm, "radius": 4 * mm});
            skArc(sketch, "E79.11", {"start": v(54.26, 47.88) * mm, "mid": v(0, 60) * mm, "end": v(-54.26, 47.88) * mm});
            skLineSegment(sketch, "E79.12", {"start": v(-60, 38.83) * mm, "end": v(-60, -38.83) * mm});
            skArc(sketch, "E79.13", {"start": v(-54.26, 47.88) * mm, "mid": v(-58.44, 44.2) * mm, "end": v(-60, 38.83) * mm});
            skLineSegment(sketch, "E79.14", {"start": v(60, 38.83) * mm, "end": v(60, -38.83) * mm});
            skArc(sketch, "E79.15", {"start": v(-54.26, -47.88) * mm, "mid": v(0, -60) * mm, "end": v(54.26, -47.88) * mm});
            skArc(sketch, "E79.16", {"start": v(-60, -38.83) * mm, "mid": v(-58.44, -44.2) * mm, "end": v(-54.26, -47.88) * mm});
            skArc(sketch, "E79.17", {"start": v(54.26, -47.88) * mm, "mid": v(58.44, -44.2) * mm, "end": v(60, -38.83) * mm});
            skArc(sketch, "E79.18", {"start": v(60, 38.83) * mm, "mid": v(58.44, 44.2) * mm, "end": v(54.26, 47.88) * mm});
            skLineSegment(sketch, "E79.19", {"start": v(-74.25, -64.25) * mm, "end": v(-74.25, 64.25) * mm});
            skLineSegment(sketch, "E80", {"start": v(-74.25, 0) * mm, "end": v(74.25, 0) * mm, "construction": true});
            skLineSegment(sketch, "E81", {"start": v(-33, 74.25) * mm, "end": v(-15, 92.25) * mm});
            skLineSegment(sketch, "E82", {"start": v(-15, 92.25) * mm, "end": v(-15, 104.25) * mm});
            skLineSegment(sketch, "E83", {"start": v(0, 74.25) * mm, "end": v(0, 104.25) * mm, "construction": true});
            skArc(sketch, "E84", {"start": v(-15, 104.25) * mm, "mid": v(0, 119.25) * mm, "end": v(15, 104.25) * mm});
            skLineSegment(sketch, "E85", {"start": v(15, 104.25) * mm, "end": v(15, 92.25) * mm});
            skLineSegment(sketch, "E86", {"start": v(15, 92.25) * mm, "end": v(33, 74.25) * mm});
            skCircle(sketch, "E87", {"center": v(0, 104.25) * mm, "radius": 6 * mm});
            skLineSegment(sketch, "E88.MirrorCS", {"start": v(-15, -92.25) * mm, "end": v(-15, -104.25) * mm});
            skLineSegment(sketch, "E89.MirrorCS", {"start": v(15, -92.25) * mm, "end": v(33, -74.25) * mm});
            skLineSegment(sketch, "E90.MirrorCS", {"start": v(-33, -74.25) * mm, "end": v(-15, -92.25) * mm});
            skLineSegment(sketch, "E91.MirrorCS", {"start": v(15, -104.25) * mm, "end": v(15, -92.25) * mm});
            skLineSegment(sketch, "E92.MirrorCS", {"start": v(0, -74.25) * mm, "end": v(0, -104.25) * mm, "construction": true});
            skArc(sketch, "E93.MirrorCS", {"start": v(-15, -104.25) * mm, "mid": v(0, -119.25) * mm, "end": v(15, -104.25) * mm});
            skCircle(sketch, "E94.MirrorC", {"center": v(0, -104.25) * mm, "radius": 6 * mm});
            skSolve(sketch);
        }
        {
            var Q0;
            {var subQ0=sQuery(id+"F16.wireOp",EDGE,"E81");Q0=makeQuery(id+"F16.imprint","IMPRINT",FACE,{"disambiguationData":[TD([[makeQuery(id+"F16.imprint","IMPRINT",EDGE,{"derivedFrom":subQ0}),-1.0]])]});}
            var Q1;
            Q1=makeQuery(id+"F16.imprint","IMPRINT",FACE,{"disambiguationData":[TD([[makeQuery(id+"F16.imprint","IMPRINT",EDGE,{"derivedFrom":sQuery(id+"F16.wireOp",EDGE,"E88.MirrorCS")}),1.0]])]});
            var Q2;
            Q2=makeQuery(id+"F2.opExtrude","CAP_FACE",FACE,{"disambiguationData":[OSD([sQuery(id+"F0.wireOp",EDGE,"E12"),sQuery(id+"F0.wireOp",EDGE,"E13"),sQuery(id+"F0.wireOp",EDGE,"E14"),sQuery(id+"F0.wireOp",EDGE,"E15"),sQuery(id+"F0.wireOp",EDGE,"E17.filletArc"),sQuery(id+"F0.wireOp",EDGE,"E18.filletArc"),sQuery(id+"F0.wireOp",EDGE,"E19.filletArc"),sQuery(id+"F0.wireOp",EDGE,"E20.filletArc"),sQuery(id+"F0.wireOp",EDGE,"E25.0"),sQuery(id+"F0.wireOp",EDGE,"E25.1"),sQuery(id+"F0.wireOp",EDGE,"E25.2"),sQuery(id+"F0.wireOp",EDGE,"E25.3"),sQuery(id+"F0.wireOp",EDGE,"E25.4"),sQuery(id+"F0.wireOp",EDGE,"E25.5"),sQuery(id+"F0.wireOp",EDGE,"E25.6"),sQuery(id+"F0.wireOp",EDGE,"E25.7")])],"isStart":false});
            extrude(context, id + "F17", {"entities" : qUnion([Q0, Q1]), "endBound" : BoundingType.UP_TO_SURFACE, "depth" : 25 * mm, "endBoundEntityFace" : qUnion([Q2]), "offsetDistance" : 25 * mm});
        }
    });
